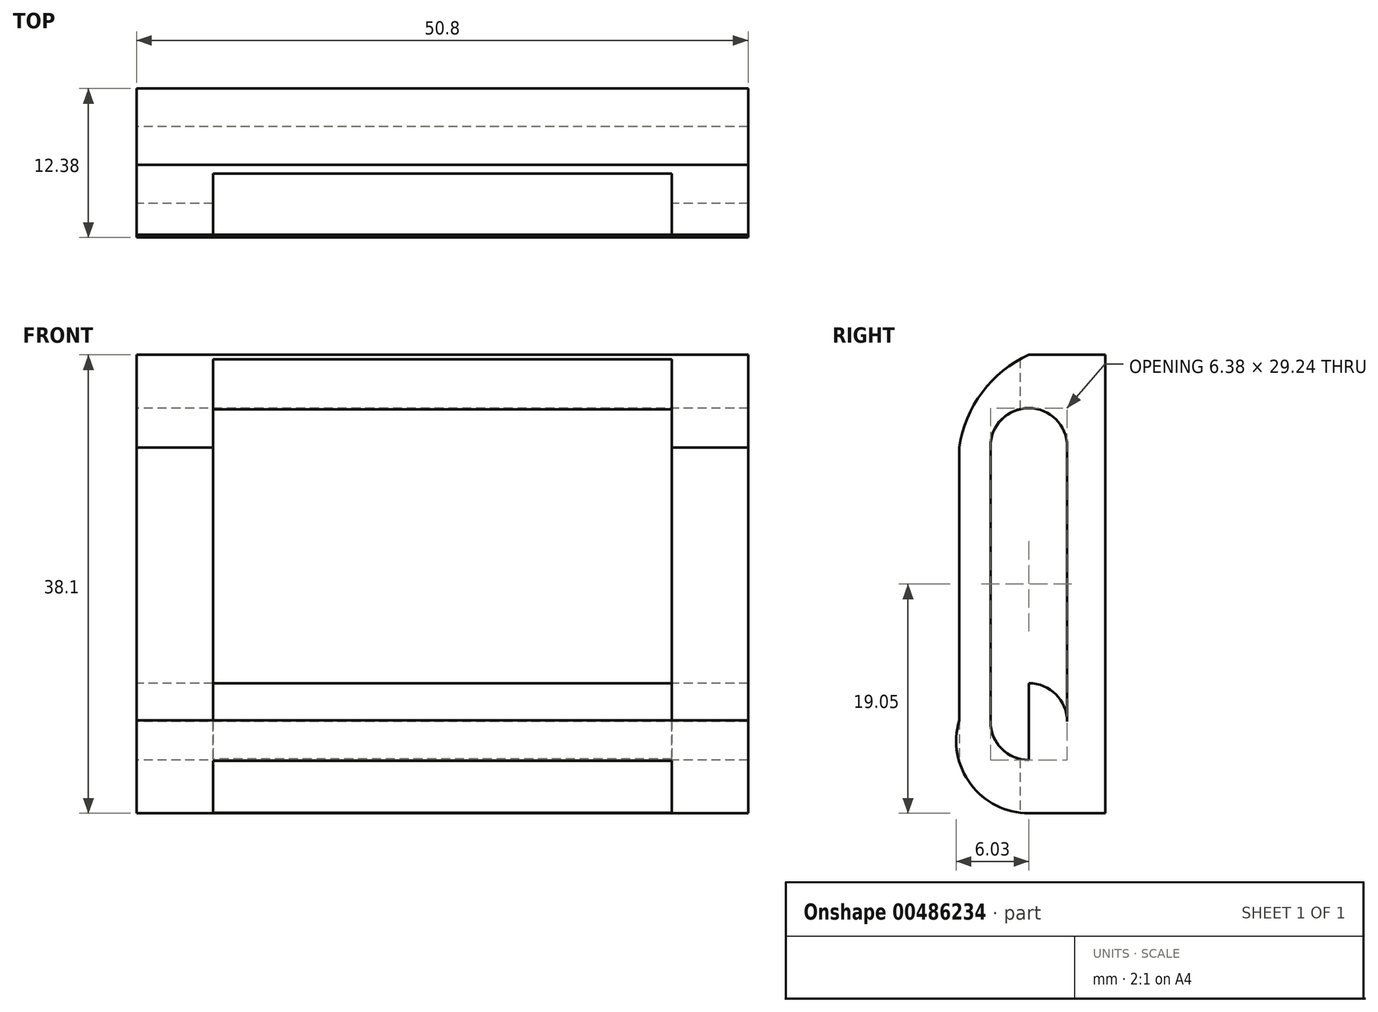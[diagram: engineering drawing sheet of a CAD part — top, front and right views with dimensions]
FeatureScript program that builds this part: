
annotation { "Feature Type Name" : "Feature", "Feature Type Description" : "" }
export const myFeature = defineFeature(function(context is Context, id is Id, definition is map)
    precondition{}
    {
        {
            var Q0;
            Q0=qCreatedBy(makeId("Front.planeOp"),FACE);
            var sketch = newSketch(context, id + "F0", { "sketchPlane" : qUnion([Q0])});
            skLineSegment(sketch, "E0.bottom", {"start": v(25.4, 19.05) * mm, "end": v(-25.4, 19.05) * mm});
            skLineSegment(sketch, "E0.top", {"start": v(25.4, -19.05) * mm, "end": v(-25.4, -19.05) * mm});
            skLineSegment(sketch, "E0.left", {"start": v(25.4, 19.05) * mm, "end": v(25.4, -19.05) * mm});
            skLineSegment(sketch, "E0.right", {"start": v(-25.4, 19.05) * mm, "end": v(-25.4, -19.05) * mm});
            skPoint(sketch, "E0.middle", {"position": v(0, 0) * mm});
            skSolve(sketch);
        }
        {
            var Q0;
            Q0 = qSketchRegion(id + "F0", true);
            extrude(context, id + "F1", {"entities" : qUnion([Q0]), "depth" : 6.35 * mm, "offsetDistance" : 25.4 * mm});
        }
        {
            var Q0;
            Q0=makeQuery(id+"F1.opExtrude","SWEPT_FACE",FACE,{"disambiguationData":[OSD([sQuery(id+"F0.wireOp",EDGE,"E0.right")])]});
            var sketch = newSketch(context, id + "F2", { "sketchPlane" : qUnion([Q0])});
            skLineSegment(sketch, "E1", {"start": v(6.35, 19.05) * mm, "end": v(6.35, 11.43) * mm, "construction": true});
            skCircle(sketch, "E2", {"center": v(6.35, 11.43) * mm, "radius": 3.19 * mm});
            skLineSegment(sketch, "E3", {"start": v(6.35, 0) * mm, "end": v(14.76, 0) * mm, "construction": true});
            skCircle(sketch, "E4.MirrorC", {"center": v(6.35, -11.43) * mm, "radius": 3.19 * mm});
            skLineSegment(sketch, "E5", {"start": v(6.35, 19.05) * mm, "end": v(3.18, 19.05) * mm});
            skLineSegment(sketch, "E6", {"start": v(3.18, 19.05) * mm, "end": v(3.16, -19.05) * mm});
            skLineSegment(sketch, "E7", {"start": v(3.16, -19.05) * mm, "end": v(6.35, -19.05) * mm});
            skArc(sketch, "E8", {"start": v(12.14, 11.34) * mm, "mid": v(10.23, 15.93) * mm, "end": v(6.35, 19.05) * mm});
            skArc(sketch, "E9", {"start": v(6.35, -19.05) * mm, "mid": v(11.17, -16.64) * mm, "end": v(12.14, -11.34) * mm});
            skLineSegment(sketch, "E10", {"start": v(12.14, 11.34) * mm, "end": v(12.14, -11.34) * mm});
            skSolve(sketch);
        }
        {
            var Q0;
            {var subQ8=sQuery(id+"F2.wireOp",EDGE,"E8");Q0=makeQuery(id+"F2.imprint","IMPRINT",FACE,{"disambiguationData":[TD([[makeQuery(id+"F2.imprint","IMPRINT",EDGE,{"derivedFrom":subQ8}),1.0]])]});}
            extrude(context, id + "F3", {"entities" : qUnion([Q0]), "operationType" : NewBodyOperationType.ADD, "oppositeDirection" : true, "depth" : 50.8 * mm, "offsetDistance" : 25.4 * mm});
        }
        {
            var Q0;
            Q0=makeQuery(id+"F1.opExtrude","SWEPT_FACE",FACE,{"disambiguationData":[OSD([sQuery(id+"F0.wireOp",EDGE,"E0.right")])]});
            var sketch = newSketch(context, id + "F4", { "sketchPlane" : qUnion([Q0])});
            skLineSegment(sketch, "E11", {"start": v(6.35, 19.05) * mm, "end": v(6.35, -19.05) * mm, "construction": true});
            skLineSegment(sketch, "E12", {"start": v(6.35, -19.05) * mm, "end": v(6.35, 19.05) * mm, "construction": true});
            skLineSegment(sketch, "E13", {"start": v(6.35, 19.05) * mm, "end": v(6.35, 11.43) * mm, "construction": true});
            skCircle(sketch, "E14", {"center": v(6.35, 11.43) * mm, "radius": 3.19 * mm});
            skLineSegment(sketch, "E15", {"start": v(6.35, 0) * mm, "end": v(24.3, 0) * mm, "construction": true});
            skCircle(sketch, "E16.MirrorC", {"center": v(6.35, -11.43) * mm, "radius": 3.19 * mm});
            skLineSegment(sketch, "E17", {"start": v(3.16, -11.43) * mm, "end": v(9.54, -11.43) * mm, "construction": true});
            skLineSegment(sketch, "E18", {"start": v(6.35, 11.43) * mm, "end": v(9.54, 11.43) * mm, "construction": true});
            skLineSegment(sketch, "E19", {"start": v(9.54, 11.43) * mm, "end": v(3.16, 11.43) * mm, "construction": true});
            skLineSegment(sketch, "E20", {"start": v(3.16, 11.43) * mm, "end": v(3.16, -11.43) * mm});
            skLineSegment(sketch, "E21", {"start": v(9.54, -11.43) * mm, "end": v(9.54, 11.43) * mm});
            skSolve(sketch);
        }
        {
            var Q0;
            {var subQ0=sQuery(id+"F4.wireOp",EDGE,"E14");var subQ1=makeQuery(id+"F4.imprint","INTERSECT",VERTEX,{"derivedFrom":[subQ0,sQuery(id+"F4.wireOp",EDGE,"E20")]});Q0=makeQuery(id+"F4.imprint","IMPRINT",FACE,{"disambiguationData":[TD([[makeQuery(id+"F4.imprint","IMPRINT",EDGE,{"disambiguationData":[TD([[subQ1,1.0]])],"derivedFrom":subQ0}),1.0]])]});}
            var Q1;
            {var subQ0=sQuery(id+"F4.wireOp",EDGE,"E14");var subQ1=makeQuery(id+"F4.imprint","INTERSECT",VERTEX,{"derivedFrom":[subQ0,sQuery(id+"F4.wireOp",EDGE,"E21")]});Q1=makeQuery(id+"F4.imprint","IMPRINT",FACE,{"disambiguationData":[TD([[makeQuery(id+"F4.imprint","IMPRINT",EDGE,{"disambiguationData":[TD([[subQ1,-1.0]])],"derivedFrom":subQ0}),1.0]])]});}
            var Q2;
            {var subQ0=sQuery(id+"F4.wireOp",EDGE,"E16.MirrorC");var subQ1=makeQuery(id+"F4.imprint","INTERSECT",VERTEX,{"derivedFrom":[subQ0,sQuery(id+"F4.wireOp",EDGE,"E20")]});Q2=makeQuery(id+"F4.imprint","IMPRINT",FACE,{"disambiguationData":[TD([[makeQuery(id+"F4.imprint","IMPRINT",EDGE,{"disambiguationData":[TD([[subQ1,1.0]])],"derivedFrom":subQ0}),-1.0]])]});}
            var Q3;
            {var subQ0=sQuery(id+"F4.wireOp",EDGE,"E16.MirrorC");var subQ1=makeQuery(id+"F4.imprint","INTERSECT",VERTEX,{"derivedFrom":[subQ0,sQuery(id+"F4.wireOp",EDGE,"E21")]});Q3=makeQuery(id+"F4.imprint","IMPRINT",FACE,{"disambiguationData":[TD([[makeQuery(id+"F4.imprint","IMPRINT",EDGE,{"disambiguationData":[TD([[subQ1,-1.0]])],"derivedFrom":subQ0}),-1.0]])]});}
            var Q4;
            {var subQ0=sQuery(id+"F4.wireOp",EDGE,"E20");Q4=makeQuery(id+"F4.imprint","IMPRINT",FACE,{"disambiguationData":[TD([[makeQuery(id+"F4.imprint","IMPRINT",EDGE,{"derivedFrom":subQ0}),1.0]])]});}
            var Q5;
            {var subQ0=sQuery(id+"F4.wireOp",EDGE,"E21");Q5=makeQuery(id+"F4.imprint","IMPRINT",FACE,{"disambiguationData":[TD([[makeQuery(id+"F4.imprint","IMPRINT",EDGE,{"derivedFrom":subQ0}),1.0]])]});}
            extrude(context, id + "F5", {"entities" : qUnion([Q0, Q1, Q2, Q3, Q4, Q5]), "operationType" : NewBodyOperationType.REMOVE, "oppositeDirection" : true, "depth" : 101.6 * mm, "offsetDistance" : 25.4 * mm});
        }
        {
            var Q0;
            Q0=makeQuery(id+"F3.opExtrude","SWEPT_FACE",FACE,{"disambiguationData":[OSD([sQuery(id+"F2.wireOp",EDGE,"E10")])]});
            var sketch = newSketch(context, id + "F6", { "sketchPlane" : qUnion([Q0])});
            skLineSegment(sketch, "E22.bottom", {"start": v(19.05, 22.23) * mm, "end": v(-19.05, 22.23) * mm});
            skLineSegment(sketch, "E22.top", {"start": v(19.05, -22.23) * mm, "end": v(-19.05, -22.23) * mm});
            skLineSegment(sketch, "E22.left", {"start": v(19.05, 22.23) * mm, "end": v(19.05, -22.23) * mm});
            skLineSegment(sketch, "E22.right", {"start": v(-19.05, 22.23) * mm, "end": v(-19.05, -22.23) * mm});
            skPoint(sketch, "E22.middle", {"position": v(0, 0) * mm});
            skSolve(sketch);
        }
        {
            var Q0;
            {var subQ0=sQuery(id+"F6.wireOp",EDGE,"E22.left");var subQ1=sQuery(id+"F2.wireOp",EDGE,"E10");var subQ2=makeQuery(id+"F3.opExtrude","SWEPT_EDGE",EDGE,{"disambiguationData":[OSD([sQuery(id+"F2.wireOp",EDGE,"E8"),subQ1])]});var subQ3=makeQuery(id+"F6.imprint","INTERSECT",VERTEX,{"derivedFrom":[subQ2,subQ0]});Q0=makeQuery(id+"F6.imprint","IMPRINT",FACE,{"disambiguationData":[TD([[makeQuery(id+"F6.imprint","IMPRINT",EDGE,{"disambiguationData":[TD([[subQ3,-1.0]])],"derivedFrom":subQ0}),-1.0]])]});}
            var Q1;
            {var subQ0=sQuery(id+"F6.wireOp",EDGE,"E22.bottom");Q1=makeQuery(id+"F6.imprint","IMPRINT",FACE,{"disambiguationData":[TD([[makeQuery(id+"F6.imprint","IMPRINT",EDGE,{"derivedFrom":subQ0}),1.0]])]});}
            var Q2;
            {var subQ0=sQuery(id+"F6.wireOp",EDGE,"E22.top");Q2=makeQuery(id+"F6.imprint","IMPRINT",FACE,{"disambiguationData":[TD([[makeQuery(id+"F6.imprint","IMPRINT",EDGE,{"derivedFrom":subQ0}),-1.0]])]});}
            extrude(context, id + "F7", {"entities" : qUnion([Q0, Q1, Q2]), "operationType" : NewBodyOperationType.REMOVE, "oppositeDirection" : true, "depth" : 5.08 * mm, "offsetDistance" : 25.4 * mm});
        }
    });
